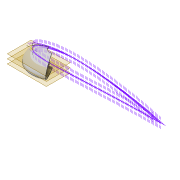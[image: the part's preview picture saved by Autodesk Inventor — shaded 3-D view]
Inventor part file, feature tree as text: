
AUTODESK INVENTOR PART (.ipt)
format: ipt  version: 2022 (Build 260153000, 153)  size: 535,040 bytes
history: native  units: mm
features: sketch x6, extrude x5, plane x3, thicken_offset x2, projected_geometry x2, shell x1, revolve x1, fillet x1
ambient origin geometry x8: Origin, YZ Plane, XZ Plane, XY Plane, X Axis, Y Axis, Z Axis, Center Point
bodies: Solid1 (feature_tree)
feature tree (21):
  extrude  "Extrusion1"  Depth=1.0mm
  shell  "Shell1"  Thickness=80.0mm
  extrude  "Extrusion16"  TaperAngle=120.0deg  [1 undecoded]
  revolve  "Revolution2"  [1 undecoded]
  extrude  "Extrusion17"  Depth=100.0mm TaperAngle=0.0deg
  plane  "Work Plane4"
  plane  "Work Plane5"
  plane  "Work Plane6"
  sketch  "Sketch41"  dims[d176=36.0mm d179=4.0mm]
  thicken_offset  "Thicken1"
  thicken_offset  "Thicken2"
  extrude  "Extrusion18"  Depth=4.0mm
  extrude  "Extrusion21"  Depth=2.2mm
  fillet  "Fillet5"  Radius=1.2mm
  sketch  "Sketch3"  dims[d0=1.0mm d1=0.0mm d2=1.0mm d159=80.0mm]
  sketch  "Sketch37"  dims[d160=10.0mm d161=0.0mm d163=120.0deg]
  sketch  "Sketch39"  dims[d164=1.0mm d165=0.0mm d166=6.454mm d167=16.2mm d168=-16.2mm]
  projected_geometry  "Projected Loop21"
  sketch  "Sketch40"  dims[d169=33.2mm d170=100.0mm d171=0.0mm]
  projected_geometry  "Projected Loop22"
  sketch  "Sketch43"  dims[d180=5.3mm d181=0.0mm d182=2.2mm d183=1.2mm d184=1.2mm d185=1.2mm d186=1.5mm]
note: 2 required parameter values undecoded (feature->parameter linkage not recoverable at this tier; creation-order binding heuristic only, values carry confidence <= 0.55)